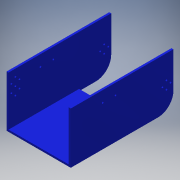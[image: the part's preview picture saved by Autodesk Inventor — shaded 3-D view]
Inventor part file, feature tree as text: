
AUTODESK INVENTOR PART (.ipt)
format: ipt  version: 2016 (Build 200138000, 138)  size: 143,872 bytes
history: native  units: in
note: dims shown in document units (in); Inventor stores cm internally (conversion verified against a paired STEP export)
features: reference x14, sketch x6, extrude x3, hole x3, fillet x1
ambient origin geometry x8: Origin, YZ Plane, XZ Plane, XY Plane, X Axis, Y Axis, Z Axis, Center Point
bodies: Solid1 (feature_tree)
feature tree (27):
  extrude  "Extrusion1"  Depth=8.0in
  extrude  "Extrusion2"  Depth=4.7in
  extrude  "Extrusion3"  Depth=2.5in
  fillet  "Fillet1"  Radius=0.15in
  hole  "Hole2"  [1 undecoded]
  hole  "Hole3"  [1 undecoded]
  hole  "Hole4"  [1 undecoded]
  sketch  "Sketch1"  dims[d0=5.0in d1=8.0in]
  sketch  "Sketch3"  dims[d2=4.0in d3=0.0in d4=4.7in]
  sketch  "Sketch4"  dims[d5=3.85in d6=0.0in d7=2.5in d8=0.15in d9=0.0in]
  sketch  "Sketch6"  dims[d10=1.2in]
  reference  "Reference1"
  reference  "Reference2"
  reference  "Reference3"
  reference  "Reference4"
  reference  "Reference5"
  reference  "Reference6"
  reference  "Reference7"
  sketch  "Sketch7"  dims[d18=0.1457in d19=0.75in d20=0.375in d21=0.25in d22=0.5635in d23=0.15in d24=0.0in]
  reference  "Reference13"
  reference  "Reference14"
  reference  "Reference15"
  reference  "Reference16"
  reference  "Reference17"
  sketch  "Sketch8"  dims[d25=0.1457in d26=0.75in d27=0.375in d28=0.25in d29=0.5635in d30=0.15in d31=0.0in d32=0.1457in d33=0.75in d34=0.375in d35=0.25in d36=0.5635in d37=1.0in d38=0.8108in]
  reference  "Reference18"
  reference  "Reference19"
note: 3 required parameter values undecoded (feature->parameter linkage not recoverable at this tier; creation-order binding heuristic only, values carry confidence <= 0.55)
